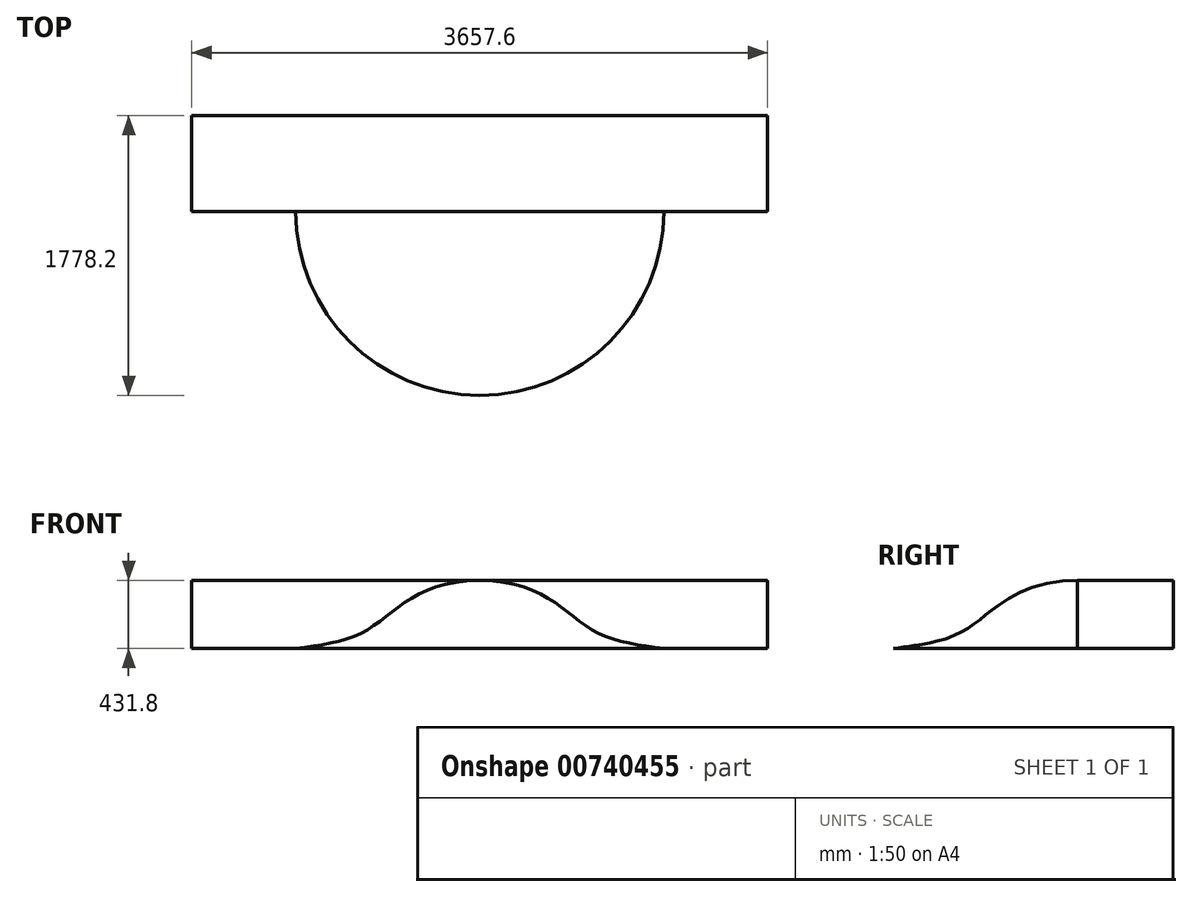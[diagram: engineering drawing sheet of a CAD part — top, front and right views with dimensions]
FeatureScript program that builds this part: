
annotation { "Feature Type Name" : "Feature", "Feature Type Description" : "" }
export const myFeature = defineFeature(function(context is Context, id is Id, definition is map)
    precondition{}
    {
        {
            var Q0;
            Q0=qCreatedBy(makeId("Top.planeOp"),FACE);
            var sketch = newSketch(context, id + "F0", { "sketchPlane" : qUnion([Q0])});
            skLineSegment(sketch, "E0.bottom", {"start": v(-1828.8, 304.8) * mm, "end": v(1828.8, 304.8) * mm});
            skLineSegment(sketch, "E0.top", {"start": v(-1828.8, -304.8) * mm, "end": v(1828.8, -304.8) * mm});
            skLineSegment(sketch, "E0.left", {"start": v(-1828.8, 304.8) * mm, "end": v(-1828.8, -304.8) * mm});
            skLineSegment(sketch, "E0.right", {"start": v(1828.8, 304.8) * mm, "end": v(1828.8, -304.8) * mm});
            skPoint(sketch, "E0.middle", {"position": v(0, 0) * mm});
            skSolve(sketch);
        }
        {
            var Q0;
            Q0=qCreatedBy(makeId("Right.planeOp"),FACE);
            var sketch = newSketch(context, id + "F1", { "sketchPlane" : qUnion([Q0])});
            skPoint(sketch, "E1.0", {"position": v(-304.8, 0) * mm});
            skLineSegment(sketch, "E2", {"start": v(-304.8, 0) * mm, "end": v(-304.8, 431.8) * mm});
            skLineSegment(sketch, "E3", {"start": v(-304.8, 0) * mm, "end": v(-1473.4, 0) * mm});
            skFitSpline(sketch, "E4", {"points": [v(-1473.4, 0) * mm, v(-1076.3, 87.35) * mm, v(-805.65, 274.54) * mm, v(-304.8, 431.8) * mm], "startDerivative": vector(1302.7, 171.1) * mm, "endDerivative": vector(1870.1, -5.58) * mm});
            skSolve(sketch);
        }
        {
            var Q0;
            Q0=makeQuery(id+"F0.imprint","IMPRINT",FACE,{"disambiguationData":[TD([[makeQuery(id+"F0.imprint","IMPRINT",EDGE,{"derivedFrom":sQuery(id+"F0.wireOp",EDGE,"E0.bottom")}),-1.0]])]});
            extrude(context, id + "F2", {"entities" : qUnion([Q0]), "depth" : 431.8 * mm, "offsetDistance" : 25 * mm});
        }
        {
            var Q0;
            Q0=makeQuery(id+"F1.imprint","IMPRINT",FACE,{"disambiguationData":[TD([[makeQuery(id+"F1.imprint","IMPRINT",EDGE,{"derivedFrom":sQuery(id+"F1.wireOp",EDGE,"E2")}),1.0]])]});
            var Q1;
            Q1=sQuery(id+"F1.wireOp",EDGE,"E2");
            revolve(context, id + "F3", {"operationType" : NewBodyOperationType.ADD, "surfaceOperationType" : NewSurfaceOperationType.NEW, "entities" : qUnion([Q0]), "axis" : qUnion([Q1]), "revolveType" : RevolveType.SYMMETRIC, "angle" : 180 * degree});
        }
    });
